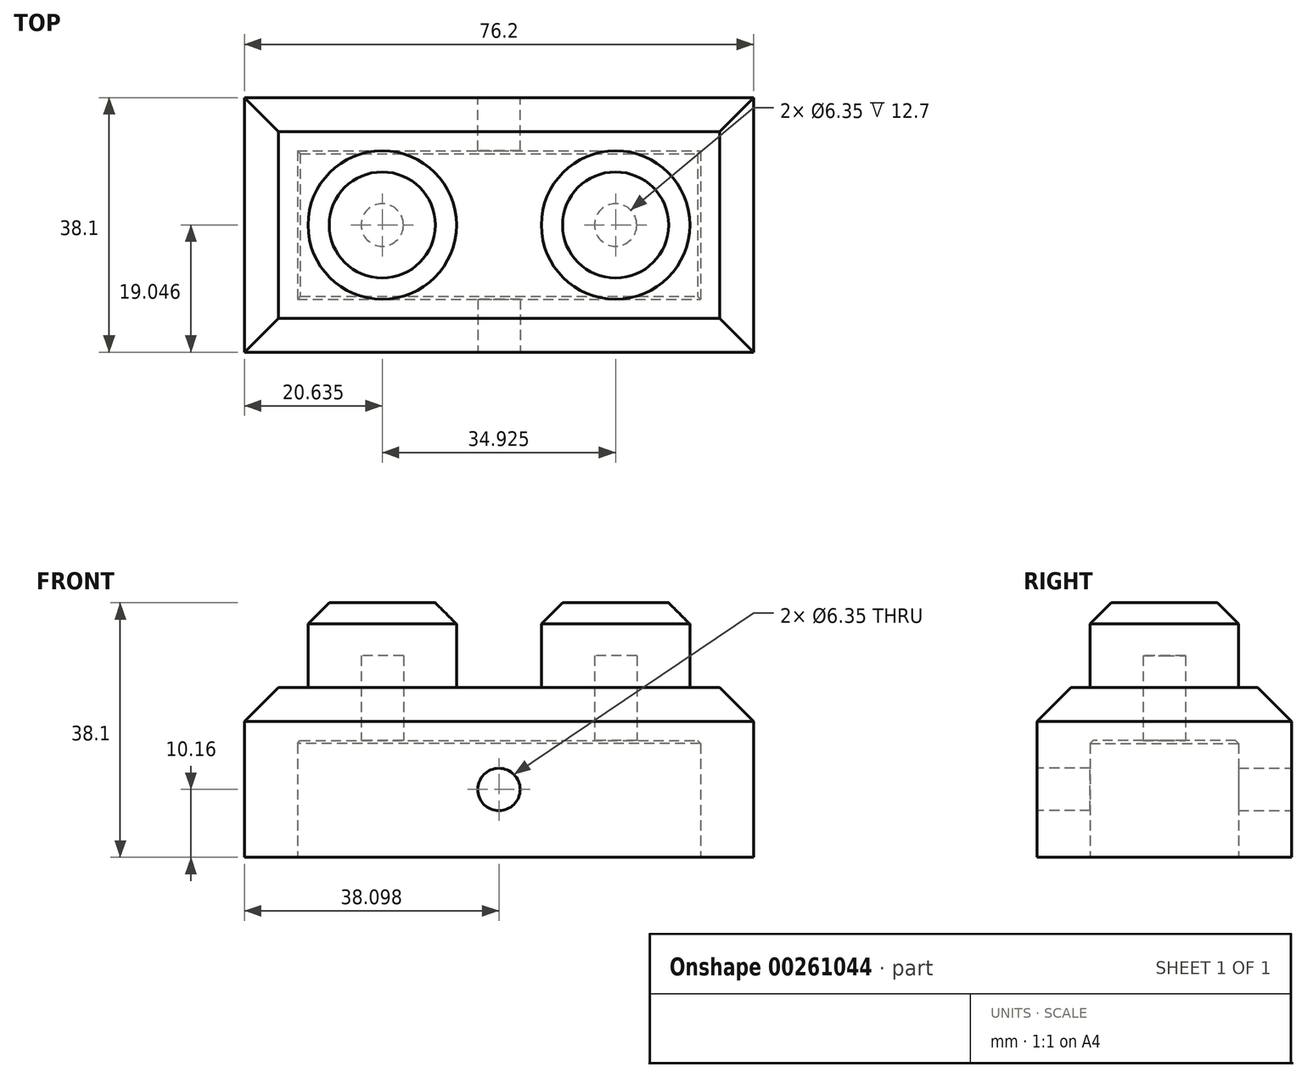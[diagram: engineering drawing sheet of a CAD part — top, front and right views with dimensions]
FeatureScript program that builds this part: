
annotation { "Feature Type Name" : "Feature", "Feature Type Description" : "" }
export const myFeature = defineFeature(function(context is Context, id is Id, definition is map)
    precondition{}
    {
        {
            var Q0;
            Q0=qCreatedBy(makeId("Top.planeOp"),FACE);
            var sketch = newSketch(context, id + "F0", { "sketchPlane" : qUnion([Q0])});
            skLineSegment(sketch, "E0.bottom", {"start": v(-50.82, 29.77) * mm, "end": v(25.38, 29.77) * mm});
            skLineSegment(sketch, "E0.top", {"start": v(-50.82, -8.33) * mm, "end": v(25.38, -8.33) * mm});
            skLineSegment(sketch, "E0.left", {"start": v(-50.82, 29.77) * mm, "end": v(-50.82, -8.33) * mm});
            skLineSegment(sketch, "E0.right", {"start": v(25.38, 29.77) * mm, "end": v(25.38, -8.33) * mm});
            skSolve(sketch);
        }
        {
            var Q0;
            Q0=qSketchRegion(id+"F0",true);
            extrude(context, id + "F1", {"entities" : qUnion([Q0]), "depth" : 25.4 * mm});
        }
        {
            var Q0;
            Q0=makeQuery(id+"F1.opExtrude","CAP_EDGE",EDGE,{"disambiguationData":[OSD([sQuery(id+"F0.wireOp",EDGE,"E0.left")])],"isStart":false});
            var Q1;
            Q1=makeQuery(id+"F1.opExtrude","CAP_FACE",FACE,{"disambiguationData":[OSD([sQuery(id+"F0.wireOp",EDGE,"E0.bottom"),sQuery(id+"F0.wireOp",EDGE,"E0.top"),sQuery(id+"F0.wireOp",EDGE,"E0.left"),sQuery(id+"F0.wireOp",EDGE,"E0.right")])],"isStart":false});
            chamfer(context, id + "F2", {"entities" : qUnion([Q0, Q1]), "width" : 5.08 * mm, "tangentPropagation" : true});
        }
        {
            var Q0;
            Q0=makeQuery(id+"F1.opExtrude","CAP_FACE",FACE,{"disambiguationData":[OSD([sQuery(id+"F0.wireOp",EDGE,"E0.bottom"),sQuery(id+"F0.wireOp",EDGE,"E0.top"),sQuery(id+"F0.wireOp",EDGE,"E0.left"),sQuery(id+"F0.wireOp",EDGE,"E0.right")])],"isStart":false});
            var sketch = newSketch(context, id + "F3", { "sketchPlane" : qUnion([Q0])});
            skCircle(sketch, "E1", {"center": v(-30.18, 10.72) * mm, "radius": 11.11 * mm});
            skCircle(sketch, "E2", {"center": v(4.74, 10.72) * mm, "radius": 11.11 * mm});
            skSolve(sketch);
        }
        {
            var Q0;
            Q0=qSketchRegion(id+"F3",true);
            extrude(context, id + "F4", {"entities" : qUnion([Q0]), "operationType" : NewBodyOperationType.ADD, "depth" : 12.7 * mm});
        }
        {
            var Q0;
            Q0=makeQuery(id+"F4.opExtrude","CAP_EDGE",EDGE,{"disambiguationData":[OSD([sQuery(id+"F3.wireOp",EDGE,"E1")])],"isStart":false});
            var Q1;
            Q1=makeQuery(id+"F4.opExtrude","CAP_EDGE",EDGE,{"disambiguationData":[OSD([sQuery(id+"F3.wireOp",EDGE,"E2")])],"isStart":false});
            chamfer(context, id + "F5", {"entities" : qUnion([Q0, Q1]), "width" : 3.17 * mm, "tangentPropagation" : true});
        }
        {
            var Q0;
            Q0=makeQuery(id+"F1.opExtrude","SWEPT_FACE",FACE,{"disambiguationData":[OSD([sQuery(id+"F0.wireOp",EDGE,"E0.top")])]});
            var sketch = newSketch(context, id + "F6", { "sketchPlane" : qUnion([Q0])});
            skCircle(sketch, "E3", {"center": v(-12.72, 10.16) * mm, "radius": 3.18 * mm});
            skSolve(sketch);
        }
        {
            var Q0;
            Q0=makeQuery(id+"F1.opExtrude","CAP_FACE",FACE,{"disambiguationData":[OSD([sQuery(id+"F0.wireOp",EDGE,"E0.bottom"),sQuery(id+"F0.wireOp",EDGE,"E0.top"),sQuery(id+"F0.wireOp",EDGE,"E0.left"),sQuery(id+"F0.wireOp",EDGE,"E0.right")])],"isStart":true});
            shell(context, id + "F7", {"entities" : qUnion([Q0]), "thickness" : 7.94 * mm});
        }
        {
            var Q0;
            Q0=qSketchRegion(id+"F6",true);
            extrude(context, id + "F8", {"entities" : qUnion([Q0]), "operationType" : NewBodyOperationType.REMOVE, "oppositeDirection" : true, "depth" : 7.94 * mm});
        }
        {
            var Q0;
            Q0=makeQuery(id+"F1.opExtrude","SWEPT_FACE",FACE,{"disambiguationData":[OSD([sQuery(id+"F0.wireOp",EDGE,"E0.bottom")])]});
            var sketch = newSketch(context, id + "F9", { "sketchPlane" : qUnion([Q0])});
            skCircle(sketch, "E4", {"center": v(12.72, 10.16) * mm, "radius": 3.18 * mm});
            skPoint(sketch, "E4.centerSnap0", {"position": v(12.72, 0) * mm});
            skSolve(sketch);
        }
        {
            var Q0;
            Q0=qSketchRegion(id+"F9",true);
            extrude(context, id + "F10", {"entities" : qUnion([Q0]), "operationType" : NewBodyOperationType.REMOVE, "oppositeDirection" : true, "depth" : 7.94 * mm});
        }
    });
